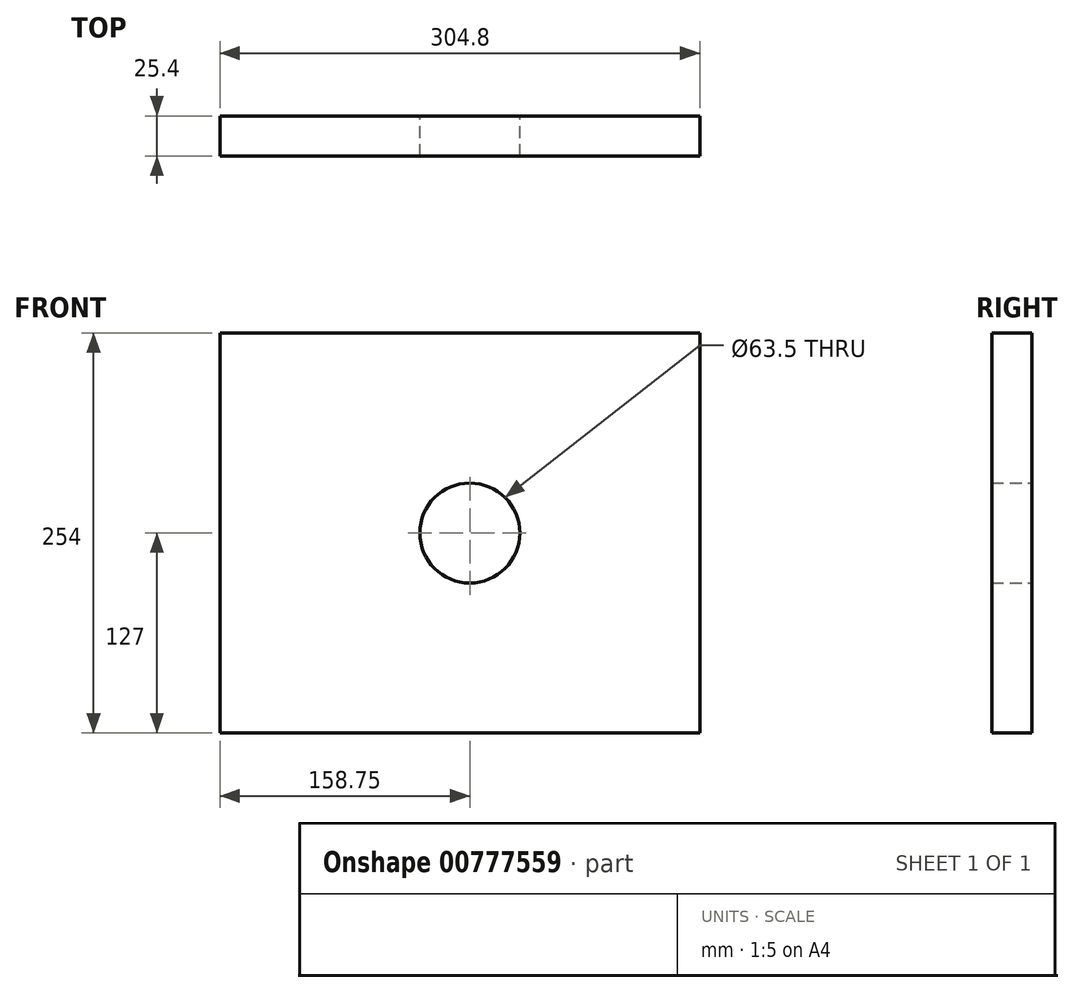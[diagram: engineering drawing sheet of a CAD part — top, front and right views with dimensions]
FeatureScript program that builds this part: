
annotation { "Feature Type Name" : "Feature", "Feature Type Description" : "" }
export const myFeature = defineFeature(function(context is Context, id is Id, definition is map)
    precondition{}
    {
        {
            var Q0;
            Q0=qCreatedBy(makeId("Front.planeOp"),FACE);
            var sketch = newSketch(context, id + "F0", { "sketchPlane" : qUnion([Q0])});
            skLineSegment(sketch, "E0.bottom", {"start": v(0, 0) * mm, "end": v(304.8, 0) * mm});
            skLineSegment(sketch, "E0.top", {"start": v(0, 254) * mm, "end": v(304.8, 254) * mm});
            skLineSegment(sketch, "E0.left", {"start": v(0, 0) * mm, "end": v(0, 254) * mm});
            skLineSegment(sketch, "E0.right", {"start": v(304.8, 0) * mm, "end": v(304.8, 254) * mm});
            skCircle(sketch, "E1", {"center": v(158.75, 127) * mm, "radius": 31.75 * mm});
            skSolve(sketch);
        }
        {
            var Q0;
            Q0 = qSketchRegion(id + "F0", true);
            extrude(context, id + "F1", {"entities" : qUnion([Q0]), "depth" : 25.4 * mm, "offsetDistance" : 25.4 * mm});
        }
    });
